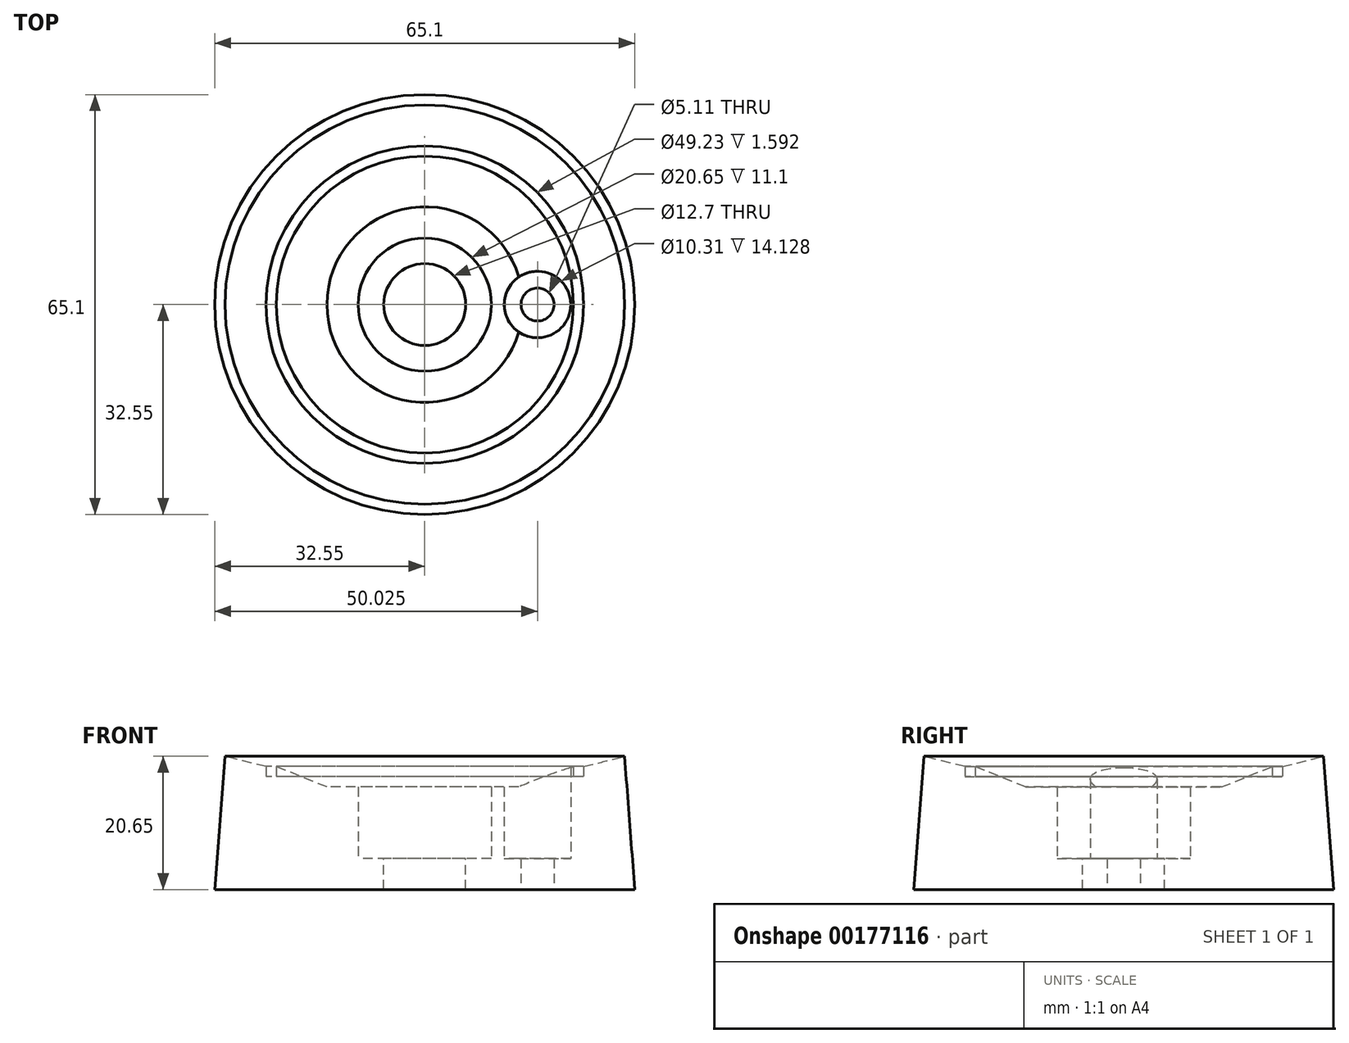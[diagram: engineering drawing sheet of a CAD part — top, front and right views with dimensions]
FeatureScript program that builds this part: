
annotation { "Feature Type Name" : "Feature", "Feature Type Description" : "" }
export const myFeature = defineFeature(function(context is Context, id is Id, definition is map)
    precondition{}
    {
        {
            var Q0;
            Q0=qCreatedBy(makeId("Top.planeOp"),FACE);
            var sketch = newSketch(context, id + "F0", { "sketchPlane" : qUnion([Q0])});
            skCircle(sketch, "E0", {"center": v(0, 0) * mm, "radius": 32.55 * mm});
            skSolve(sketch);
        }
        {
            var Q0;
            Q0=qCreatedBy(makeId("Top.planeOp"),FACE);
            cPlane(context, id + "F1", {"entities" : qUnion([Q0]), "cplaneType" : CPlaneType.OFFSET, "offset" : 20.65 * mm, "width" : 152.4 * mm, "height" : 152.4 * mm});
        }
        {
            var Q0;
            Q0=qCreatedBy(id+"F1.planeOp",FACE);
            var sketch = newSketch(context, id + "F2", { "sketchPlane" : qUnion([Q0])});
            skCircle(sketch, "E1", {"center": v(0, 0) * mm, "radius": 30.96 * mm});
            skSolve(sketch);
        }
        {
            var Q0;
            Q0=makeQuery(id+"F0.imprint","IMPRINT",FACE,{"disambiguationData":[TD([[makeQuery(id+"F0.imprint","IMPRINT",EDGE,{"derivedFrom":sQuery(id+"F0.wireOp",EDGE,"E0")}),1.0]])]});
            var Q1;
            Q1=makeQuery(id+"F2.imprint","IMPRINT",FACE,{"disambiguationData":[TD([[makeQuery(id+"F2.imprint","IMPRINT",EDGE,{"derivedFrom":sQuery(id+"F2.wireOp",EDGE,"E1")}),1.0]])]});
            loft(context, id + "F3", {"sheetProfilesArray" : [{ "sheetProfileEntities" : qUnion([Q0]) }, { "sheetProfileEntities" : qUnion([Q1]) }]});
        }
        {
            var Q0;
            Q0=qCreatedBy(makeId("Front.planeOp"),FACE);
            var sketch = newSketch(context, id + "F4", { "sketchPlane" : qUnion([Q0])});
            skLineSegment(sketch, "E2.bottom", {"start": v(0, 20.65) * mm, "end": v(30.96, 20.65) * mm});
            skLineSegment(sketch, "E2.top", {"start": v(0, 19.06) * mm, "end": v(24.6, 19.06) * mm});
            skLineSegment(sketch, "E2.left", {"start": v(0, 20.65) * mm, "end": v(0, 19.06) * mm});
            skLineSegment(sketch, "E3", {"start": v(30.96, 20.65) * mm, "end": v(24.6, 19.06) * mm});
            skSolve(sketch);
        }
        {
            var Q0;
            Q0 = qSketchRegion(id + "F4", true);
            var Q1;
            Q1=makeQuery(id+"F3.opLoft","SWEPT_FACE",FACE,{"disambiguationData":[OSD([sQuery(id+"F0.wireOp",EDGE,"E0"),sQuery(id+"F2.wireOp",EDGE,"E1")])]});
            revolve(context, id + "F5", {"entities" : qUnion([Q0]), "axis" : qUnion([Q1]), "revolveType" : RevolveType.FULL});
        }
        {
            var Q0;
            Q0=makeQuery(id+"F5.opRevolve","SWEPT_BODY",BODY,{"disambiguationData":[OSD([sQuery(id+"F4.wireOp",EDGE,"E2.bottom"),sQuery(id+"F4.wireOp",EDGE,"E2.top"),sQuery(id+"F4.wireOp",EDGE,"E2.left"),sQuery(id+"F4.wireOp",EDGE,"E3")])]});
            var Q1;
            Q1=makeQuery(id+"F3.opLoft","SWEPT_BODY",BODY,{"disambiguationData":[OSD([makeQuery(id+"F0.imprint","IMPRINT",FACE,{"disambiguationData":[TD([[makeQuery(id+"F0.imprint","IMPRINT",EDGE,{"derivedFrom":sQuery(id+"F0.wireOp",EDGE,"E0")}),1.0]])]}),makeQuery(id+"F2.imprint","IMPRINT",FACE,{"disambiguationData":[TD([[makeQuery(id+"F2.imprint","IMPRINT",EDGE,{"derivedFrom":sQuery(id+"F2.wireOp",EDGE,"E1")}),1.0]])]})])]});
            booleanBodies(context, id + "F6", {"operationType" : BooleanOperationType.SUBTRACTION, "tools" : qUnion([Q0]), "targets" : qUnion([Q1])});
        }
        {
            var Q0;
            Q0=makeQuery(id+"F6.opBoolean","COPY",FACE,{"derivedFrom":makeQuery(id+"F5.opRevolve","SWEPT_FACE",FACE,{"disambiguationData":[OSD([sQuery(id+"F4.wireOp",EDGE,"E2.top")])]})});
            var sketch = newSketch(context, id + "F7", { "sketchPlane" : qUnion([Q0])});
            skCircle(sketch, "E4", {"center": v(0, 0) * mm, "radius": 24.61 * mm});
            skCircle(sketch, "E5", {"center": v(0, 0) * mm, "radius": 23.03 * mm});
            skSolve(sketch);
        }
        {
            var Q0;
            Q0 = qSketchRegion(id + "F7", true);
            extrude(context, id + "F8", {"entities" : qUnion([Q0]), "endBound" : BoundingType.SYMMETRIC, "depth" : 3.17 * mm});
        }
        {
            var Q0;
            Q0=makeQuery(id+"F8.opExtrude","SWEPT_BODY",BODY,{"disambiguationData":[OSD([sQuery(id+"F7.wireOp",EDGE,"E4"),sQuery(id+"F7.wireOp",EDGE,"E5")])]});
            var Q1;
            Q1=makeQuery(id+"F3.opLoft","SWEPT_BODY",BODY,{"disambiguationData":[OSD([makeQuery(id+"F0.imprint","IMPRINT",FACE,{"disambiguationData":[TD([[makeQuery(id+"F0.imprint","IMPRINT",EDGE,{"derivedFrom":sQuery(id+"F0.wireOp",EDGE,"E0")}),1.0]])]}),makeQuery(id+"F2.imprint","IMPRINT",FACE,{"disambiguationData":[TD([[makeQuery(id+"F2.imprint","IMPRINT",EDGE,{"derivedFrom":sQuery(id+"F2.wireOp",EDGE,"E1")}),1.0]])]})])]});
            booleanBodies(context, id + "F9", {"operationType" : BooleanOperationType.SUBTRACTION, "tools" : qUnion([Q0]), "targets" : qUnion([Q1])});
        }
        {
            var Q0;
            Q0=qCreatedBy(makeId("Front.planeOp"),FACE);
            var sketch = newSketch(context, id + "F10", { "sketchPlane" : qUnion([Q0])});
            skLineSegment(sketch, "E6.bottom", {"start": v(0, 19.06) * mm, "end": v(23.03, 19.06) * mm});
            skLineSegment(sketch, "E6.top", {"start": v(0, 15.89) * mm, "end": v(15.17, 15.89) * mm});
            skLineSegment(sketch, "E6.left", {"start": v(0, 19.06) * mm, "end": v(0, 15.89) * mm});
            skLineSegment(sketch, "E7", {"start": v(23.03, 19.06) * mm, "end": v(15.17, 15.89) * mm});
            skSolve(sketch);
        }
        {
            var Q0;
            Q0 = qSketchRegion(id + "F10", true);
            var Q1;
            Q1=makeQuery(id+"F3.opLoft","SWEPT_FACE",FACE,{"disambiguationData":[OSD([sQuery(id+"F0.wireOp",EDGE,"E0"),sQuery(id+"F2.wireOp",EDGE,"E1")])]});
            revolve(context, id + "F11", {"entities" : qUnion([Q0]), "axis" : qUnion([Q1]), "revolveType" : RevolveType.FULL});
        }
        {
            var Q0;
            Q0=makeQuery(id+"F11.opRevolve","SWEPT_BODY",BODY,{"disambiguationData":[OSD([sQuery(id+"F10.wireOp",EDGE,"E6.bottom"),sQuery(id+"F10.wireOp",EDGE,"E6.top"),sQuery(id+"F10.wireOp",EDGE,"E6.left"),sQuery(id+"F10.wireOp",EDGE,"E7")])]});
            var Q1;
            Q1=makeQuery(id+"F3.opLoft","SWEPT_BODY",BODY,{"disambiguationData":[OSD([makeQuery(id+"F0.imprint","IMPRINT",FACE,{"disambiguationData":[TD([[makeQuery(id+"F0.imprint","IMPRINT",EDGE,{"derivedFrom":sQuery(id+"F0.wireOp",EDGE,"E0")}),1.0]])]}),makeQuery(id+"F2.imprint","IMPRINT",FACE,{"disambiguationData":[TD([[makeQuery(id+"F2.imprint","IMPRINT",EDGE,{"derivedFrom":sQuery(id+"F2.wireOp",EDGE,"E1")}),1.0]])]})])]});
            booleanBodies(context, id + "F12", {"operationType" : BooleanOperationType.SUBTRACTION, "tools" : qUnion([Q0]), "targets" : qUnion([Q1])});
        }
        {
            var Q0;
            Q0=makeQuery(id+"F12.opBoolean","COPY",FACE,{"derivedFrom":makeQuery(id+"F11.opRevolve","SWEPT_FACE",FACE,{"disambiguationData":[OSD([sQuery(id+"F10.wireOp",EDGE,"E6.top")])]})});
            var sketch = newSketch(context, id + "F13", { "sketchPlane" : qUnion([Q0])});
            skCircle(sketch, "E8", {"center": v(0, 0) * mm, "radius": 10.33 * mm});
            skSolve(sketch);
        }
        {
            var Q0;
            Q0 = qSketchRegion(id + "F13", true);
            extrude(context, id + "F14", {"entities" : qUnion([Q0]), "endBound" : BoundingType.SYMMETRIC, "depth" : 22.2 * mm});
        }
        {
            var Q0;
            Q0=makeQuery(id+"F14.opExtrude","SWEPT_BODY",BODY,{"disambiguationData":[OSD([sQuery(id+"F13.wireOp",EDGE,"E8")])]});
            var Q1;
            Q1=makeQuery(id+"F3.opLoft","SWEPT_BODY",BODY,{"disambiguationData":[OSD([makeQuery(id+"F0.imprint","IMPRINT",FACE,{"disambiguationData":[TD([[makeQuery(id+"F0.imprint","IMPRINT",EDGE,{"derivedFrom":sQuery(id+"F0.wireOp",EDGE,"E0")}),1.0]])]}),makeQuery(id+"F2.imprint","IMPRINT",FACE,{"disambiguationData":[TD([[makeQuery(id+"F2.imprint","IMPRINT",EDGE,{"derivedFrom":sQuery(id+"F2.wireOp",EDGE,"E1")}),1.0]])]})])]});
            booleanBodies(context, id + "F15", {"operationType" : BooleanOperationType.SUBTRACTION, "tools" : qUnion([Q0]), "targets" : qUnion([Q1])});
        }
        {
            var Q0;
            Q0=makeQuery(id+"F15.opBoolean","COPY",FACE,{"derivedFrom":makeQuery(id+"F14.opExtrude","CAP_FACE",FACE,{"disambiguationData":[OSD([sQuery(id+"F13.wireOp",EDGE,"E8")])],"isStart":true})});
            var sketch = newSketch(context, id + "F16", { "sketchPlane" : qUnion([Q0])});
            skPoint(sketch, "E9", {"position": v(0, 0) * mm});
            skSolve(sketch);
        }
        {
            var Q0;
            Q0=sQuery(id+"F16.wireOp",VERTEX,"E9");
            var Q1;
            Q1=makeQuery(id+"F3.opLoft","SWEPT_BODY",BODY,{"disambiguationData":[OSD([makeQuery(id+"F0.imprint","IMPRINT",FACE,{"disambiguationData":[TD([[makeQuery(id+"F0.imprint","IMPRINT",EDGE,{"derivedFrom":sQuery(id+"F0.wireOp",EDGE,"E0")}),1.0]])]}),makeQuery(id+"F2.imprint","IMPRINT",FACE,{"disambiguationData":[TD([[makeQuery(id+"F2.imprint","IMPRINT",EDGE,{"derivedFrom":sQuery(id+"F2.wireOp",EDGE,"E1")}),1.0]])]})])]});
            hole(context, id + "F17", {"style" : HoleStyle.SIMPLE, "endStyle" : HoleEndStyle.THROUGH, "holeDiameter" : 12.7 * mm, "startFromSketch" : true, "locations" : qUnion([Q0]), "scope" : qUnion([Q1]), "isTappedThrough" : true});
        }
        {
            var Q0;
            Q0=qCreatedBy(id+"F1.planeOp",FACE);
            var sketch = newSketch(context, id + "F18", { "sketchPlane" : qUnion([Q0])});
            skCircle(sketch, "E10", {"center": v(17.48, 0) * mm, "radius": 2.55 * mm});
            skSolve(sketch);
        }
        {
            var Q0;
            Q0 = qSketchRegion(id + "F18", true);
            extrude(context, id + "F19", {"entities" : qUnion([Q0]), "endBound" : BoundingType.SYMMETRIC, "depth" : 50.8 * mm});
        }
        {
            var Q0;
            Q0=makeQuery(id+"F19.opExtrude","SWEPT_BODY",BODY,{"disambiguationData":[OSD([sQuery(id+"F18.wireOp",EDGE,"E10")])]});
            var Q1;
            Q1=makeQuery(id+"F3.opLoft","SWEPT_BODY",BODY,{"disambiguationData":[OSD([makeQuery(id+"F0.imprint","IMPRINT",FACE,{"disambiguationData":[TD([[makeQuery(id+"F0.imprint","IMPRINT",EDGE,{"derivedFrom":sQuery(id+"F0.wireOp",EDGE,"E0")}),1.0]])]}),makeQuery(id+"F2.imprint","IMPRINT",FACE,{"disambiguationData":[TD([[makeQuery(id+"F2.imprint","IMPRINT",EDGE,{"derivedFrom":sQuery(id+"F2.wireOp",EDGE,"E1")}),1.0]])]})])]});
            booleanBodies(context, id + "F20", {"operationType" : BooleanOperationType.SUBTRACTION, "tools" : qUnion([Q0]), "targets" : qUnion([Q1])});
        }
        {
            var Q0;
            Q0=qCreatedBy(makeId("Top.planeOp"),FACE);
            var sketch = newSketch(context, id + "F21", { "sketchPlane" : qUnion([Q0])});
            skCircle(sketch, "E11", {"center": v(17.48, 0) * mm, "radius": 5.16 * mm});
            skSolve(sketch);
        }
        {
            var Q0;
            Q0 = qSketchRegion(id + "F21", true);
            extrude(context, id + "F22", {"entities" : qUnion([Q0]), "depth" : 25.4 * mm});
        }
        {
            var Q0;
            Q0=makeQuery(id+"F22.opExtrude","SWEPT_BODY",BODY,{"disambiguationData":[OSD([sQuery(id+"F21.wireOp",EDGE,"E11")])]});
            transform(context, id + "F23", {"entities" : qUnion([Q0]), "transformType" : TransformType.TRANSLATION_3D, "dx" : 0 * mm, "dy" : 0 * mm, "dz" : 4.78 * mm, "makeCopy" : false});
        }
        {
            var Q0;
            Q0=makeQuery(id+"F22.opExtrude","SWEPT_BODY",BODY,{"disambiguationData":[OSD([sQuery(id+"F21.wireOp",EDGE,"E11")])]});
            var Q1;
            Q1=makeQuery(id+"F3.opLoft","SWEPT_BODY",BODY,{"disambiguationData":[OSD([makeQuery(id+"F0.imprint","IMPRINT",FACE,{"disambiguationData":[TD([[makeQuery(id+"F0.imprint","IMPRINT",EDGE,{"derivedFrom":sQuery(id+"F0.wireOp",EDGE,"E0")}),1.0]])]}),makeQuery(id+"F2.imprint","IMPRINT",FACE,{"disambiguationData":[TD([[makeQuery(id+"F2.imprint","IMPRINT",EDGE,{"derivedFrom":sQuery(id+"F2.wireOp",EDGE,"E1")}),1.0]])]})])]});
            booleanBodies(context, id + "F24", {"operationType" : BooleanOperationType.SUBTRACTION, "tools" : qUnion([Q0]), "targets" : qUnion([Q1])});
        }
    });
